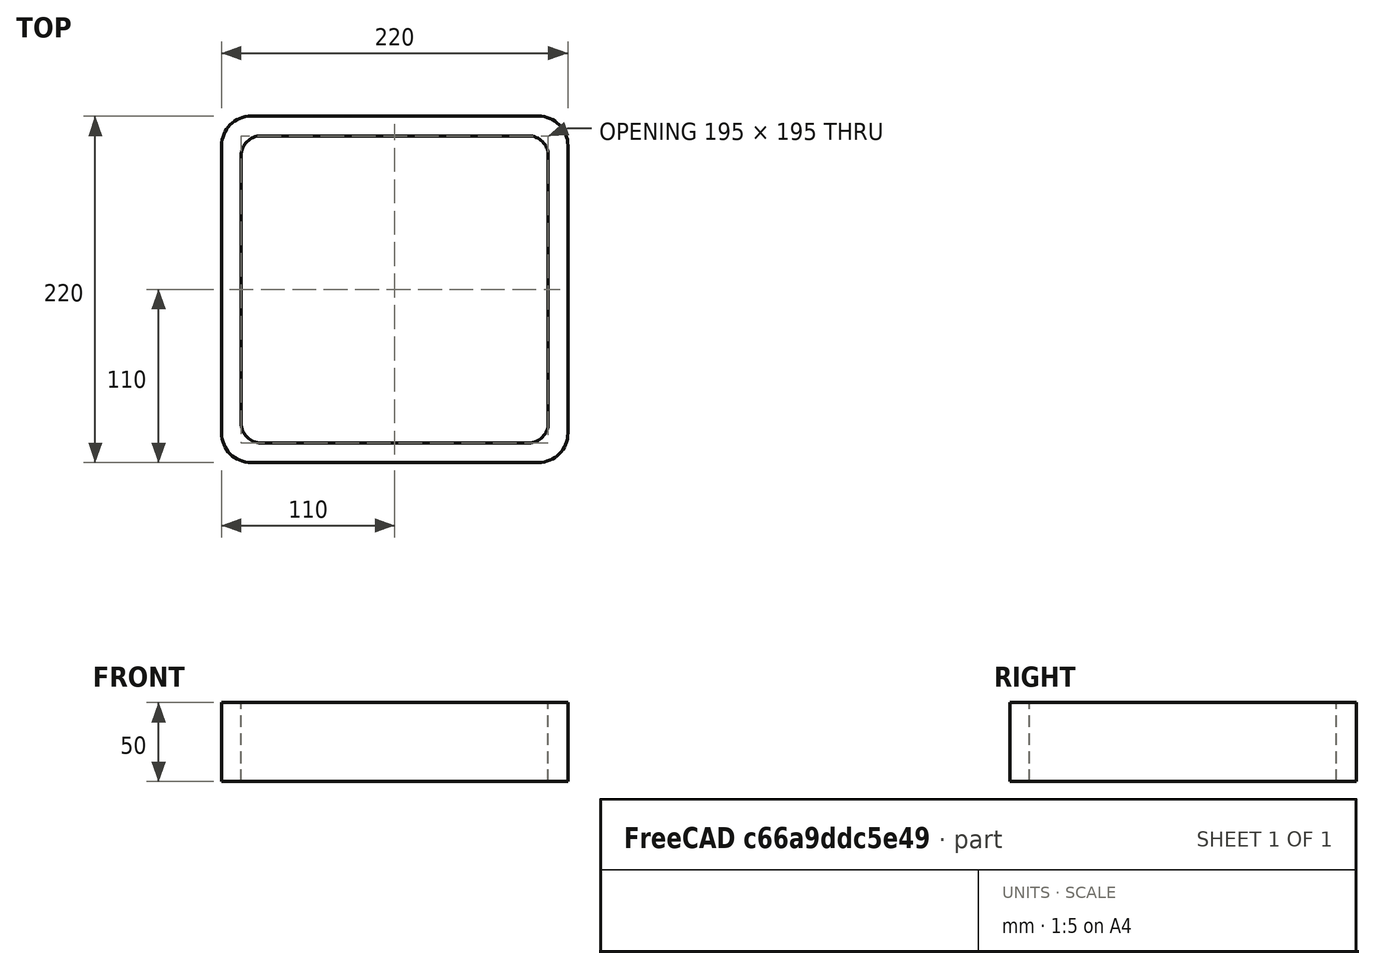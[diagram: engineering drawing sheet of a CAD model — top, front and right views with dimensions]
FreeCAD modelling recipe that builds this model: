
FCSTD DOCUMENT  (FreeCAD 0.15R4671 (Git))
Label: Square hollow section 220x220x12.5 EN10219 S235JRH
License: All rights reserved
LicenseURL: http://en.wikipedia.org/wiki/All_rights_reserved
objects: Sketcher::SketchObject×1, Part::Extrusion×1
note: 2 computed .brp shape members not serialized (recipe doc carries the construction recipe); baked Part::Feature solids carry a one-line shape summary decoded from their .brp

FEATURE [Sketcher::SketchObject] Sketch
  sketch-geometry (16):
    g0: LineSegment StartX=-85 StartY=97.5 StartZ=0 EndX=85 EndY=97.5 EndZ=0
    g1: LineSegment StartX=97.5 StartY=85 StartZ=0 EndX=97.5 EndY=-85 EndZ=0
    g2: LineSegment StartX=85 StartY=-97.5 StartZ=0 EndX=-85 EndY=-97.5 EndZ=0
    g3: LineSegment StartX=-97.5 StartY=-85 StartZ=0 EndX=-97.5 EndY=85 EndZ=0
    g4: LineSegment StartX=-91.25 StartY=110 StartZ=0 EndX=91.25 EndY=110 EndZ=0
    g5: LineSegment StartX=110 StartY=91.25 StartZ=0 EndX=110 EndY=-91.25 EndZ=0
    g6: LineSegment StartX=91.25 StartY=-110 StartZ=0 EndX=-91.25 EndY=-110 EndZ=0
    g7: LineSegment StartX=-110 StartY=-91.25 StartZ=0 EndX=-110 EndY=91.25 EndZ=0
    g8: ArcOfCircle CenterX=-85 CenterY=85 CenterZ=0 NormalX=0 NormalY=0 NormalZ=1 Radius=12.5 StartAngle=1.5708 EndAngle=3.14159
    g9: ArcOfCircle CenterX=85 CenterY=85 CenterZ=0 NormalX=0 NormalY=0 NormalZ=1 Radius=12.5 StartAngle=0 EndAngle=1.5708
    g10: ArcOfCircle CenterX=85 CenterY=-85 CenterZ=0 NormalX=0 NormalY=0 NormalZ=1 Radius=12.5 StartAngle=4.71239 EndAngle=6.28319
    g11: ArcOfCircle CenterX=-85 CenterY=-85 CenterZ=0 NormalX=0 NormalY=0 NormalZ=1 Radius=12.5 StartAngle=3.14159 EndAngle=4.71239
    g12: ArcOfCircle CenterX=91.25 CenterY=91.25 CenterZ=0 NormalX=0 NormalY=0 NormalZ=1 Radius=18.75 StartAngle=0 EndAngle=1.5708
    g13: ArcOfCircle CenterX=91.25 CenterY=-91.25 CenterZ=0 NormalX=0 NormalY=0 NormalZ=1 Radius=18.75 StartAngle=4.71239 EndAngle=6.28319
    g14: ArcOfCircle CenterX=-91.25 CenterY=-91.25 CenterZ=0 NormalX=0 NormalY=0 NormalZ=1 Radius=18.75 StartAngle=3.14159 EndAngle=4.71239
    g15: ArcOfCircle CenterX=-91.25 CenterY=91.25 CenterZ=0 NormalX=0 NormalY=0 NormalZ=1 Radius=18.75 StartAngle=1.5708 EndAngle=3.14159
  constraints (36):
    c: Horizontal(g2)
    c: Vertical(g3)
    c: Horizontal(g6)
    c: Vertical(g7)
    c: Tangent(g3,g8) = 1.5708
    c: Tangent(g0,g8) = 1.5708
    c: Tangent(g0,g9) = 1.5708
    c: Tangent(g1,g9) = 1.5708
    c: Tangent(g1,g10) = 1.5708
    c: Tangent(g2,g10) = 1.5708
    c: Tangent(g2,g11) = 1.5708
    c: Tangent(g3,g11) = 1.5708
    c: Tangent(g4,g12) = 1.5708
    c: Tangent(g5,g12) = 1.5708
    c: Tangent(g5,g13) = 1.5708
    c: Tangent(g6,g13) = 1.5708
    c: Tangent(g6,g14) = 1.5708
    c: Tangent(g7,g14) = 1.5708
    c: Tangent(g7,g15) = 1.5708
    c: Tangent(g4,g15) = 1.5708
    c: Equal(g9,g8)
    c: Equal(g9,g11)
    c: Equal(g9,g10)
    c: Equal(g12,g15)
    c: Equal(g12,g14)
    c: Equal(g12,g13)
    c: Symmetric(g4,g6,g-1)
    c: Symmetric(g7,g5,g-2)
    c: DistanceY(g4,g6) = -220
    c: DistanceX(g7,g5) = 220
    c: Symmetric(g3,g1,g-2)
    c: Symmetric(g0,g2,g-1)
    c: DistanceY(g0,g4) = 12.5
    c: DistanceX(g5,g1) = -12.5
    c: Radius(g9) = 12.5
    c: Radius(g12) = 18.75
FEATURE [Part::Extrusion] Extrude  label="Square hollow section 220x220x12.5 EN10219 S235JRH"
  Base = -> Sketch
  Dir = (0,0,50)
  Solid = true
